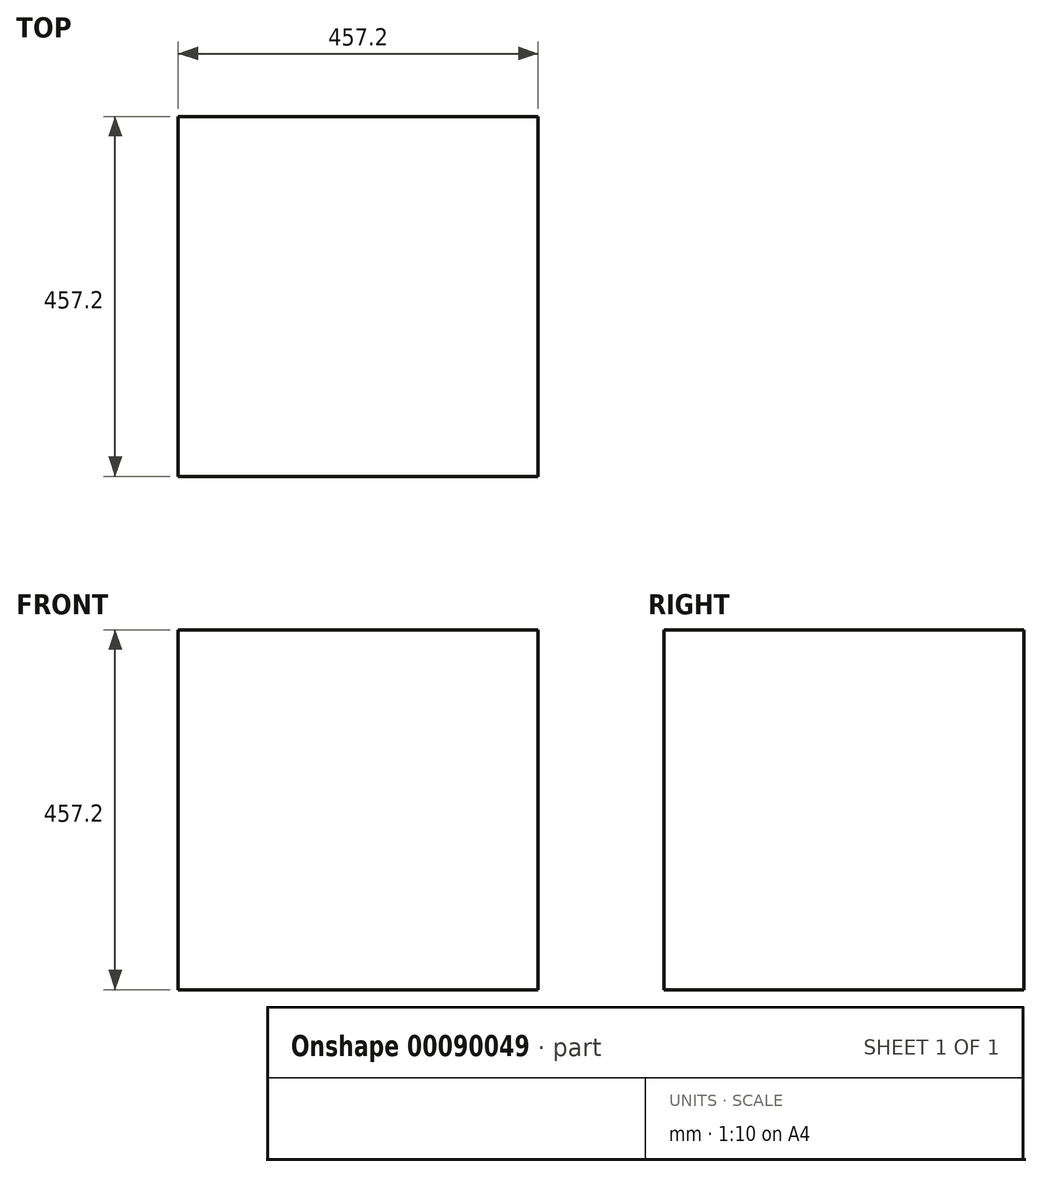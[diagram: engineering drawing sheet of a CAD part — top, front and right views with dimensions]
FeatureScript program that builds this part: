
annotation { "Feature Type Name" : "Feature", "Feature Type Description" : "" }
export const myFeature = defineFeature(function(context is Context, id is Id, definition is map)
    precondition{}
    {
        {
            var Q0;
            Q0=qCreatedBy(makeId("Top.planeOp"),FACE);
            var sketch = newSketch(context, id + "F0", { "sketchPlane" : qUnion([Q0])});
            skLineSegment(sketch, "E0.rect.bottom", {"start": v(228.6, 229.13) * mm, "end": v(-228.6, 229.13) * mm});
            skLineSegment(sketch, "E0.rect.top", {"start": v(228.6, -228.07) * mm, "end": v(-228.6, -228.07) * mm});
            skLineSegment(sketch, "E0.rect.left", {"start": v(228.6, 229.13) * mm, "end": v(228.6, -228.07) * mm});
            skLineSegment(sketch, "E0.rect.right", {"start": v(-228.6, 229.13) * mm, "end": v(-228.6, -228.07) * mm});
            skPoint(sketch, "E0.rect.middle", {"position": v(0, 0.53) * mm});
            skSolve(sketch);
        }
        {
            var Q0;
            Q0=qSketchRegion(id+"F0",true);
            extrude(context, id + "F1", {"entities" : qUnion([Q0]), "depth" : 457.2 * mm});
        }
    });
